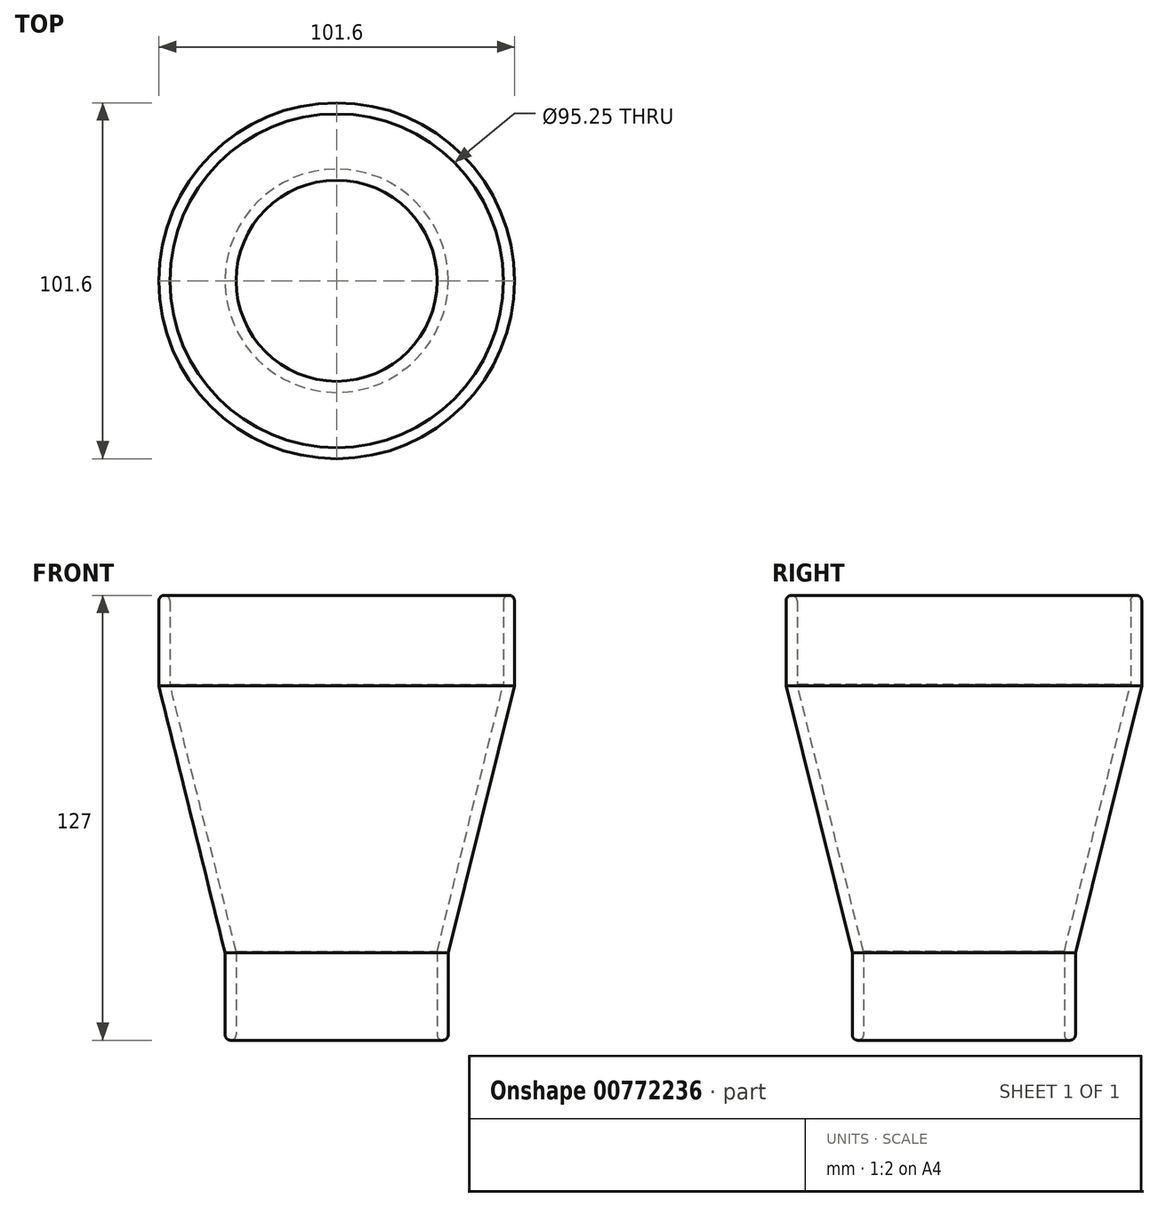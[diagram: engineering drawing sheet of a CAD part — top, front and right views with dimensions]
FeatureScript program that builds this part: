
annotation { "Feature Type Name" : "Feature", "Feature Type Description" : "" }
export const myFeature = defineFeature(function(context is Context, id is Id, definition is map)
    precondition{}
    {
        {
            var Q0;
            Q0=qCreatedBy(makeId("Front.planeOp"),FACE);
            var sketch = newSketch(context, id + "F0", { "sketchPlane" : qUnion([Q0])});
            skLineSegment(sketch, "E0", {"start": v(0, 0) * mm, "end": v(0, 101.6) * mm});
            skLineSegment(sketch, "E1", {"start": v(0, 0) * mm, "end": v(31.88, 0) * mm});
            skLineSegment(sketch, "E2", {"start": v(0, 101.6) * mm, "end": v(47.63, 101.6) * mm});
            skLineSegment(sketch, "E3", {"start": v(28.7, 0) * mm, "end": v(28.7, 25.4) * mm});
            skLineSegment(sketch, "E4", {"start": v(28.7, 25.4) * mm, "end": v(47.63, 101.6) * mm});
            skLineSegment(sketch, "E5", {"start": v(47.63, 101.6) * mm, "end": v(47.63, 127) * mm});
            skLineSegment(sketch, "E6", {"start": v(50.8, 127) * mm, "end": v(0, 127) * mm});
            skLineSegment(sketch, "E7", {"start": v(0, 127) * mm, "end": v(0, 101.6) * mm});
            skLineSegment(sketch, "E8.0", {"start": v(50.8, 101.21) * mm, "end": v(50.8, 127) * mm});
            skLineSegment(sketch, "E8.1", {"start": v(31.88, 25.01) * mm, "end": v(50.8, 101.21) * mm});
            skLineSegment(sketch, "E8.2", {"start": v(31.88, 0) * mm, "end": v(31.88, 25.01) * mm});
            skSolve(sketch);
        }
        {
            var Q0;
            {var subQ1=sQuery(id+"F0.wireOp",EDGE,"E3");Q0=makeQuery(id+"F0.imprint","IMPRINT",FACE,{"disambiguationData":[TD([[makeQuery(id+"F0.imprint","IMPRINT",EDGE,{"derivedFrom":subQ1}),-1.0]])]});}
            var Q1;
            Q1=sQuery(id+"F0.wireOp",EDGE,"E0");
            revolve(context, id + "F1", {"surfaceOperationType" : NewSurfaceOperationType.NEW, "entities" : qUnion([Q0]), "axis" : qUnion([Q1]), "revolveType" : RevolveType.FULL});
        }
        {
            var Q0;
            Q0=qCreatedBy(makeId("Right.planeOp"),FACE);
            var sketch = newSketch(context, id + "F2", { "sketchPlane" : qUnion([Q0])});
            skLineSegment(sketch, "E9", {"start": v(9.53, 0) * mm, "end": v(9.53, 10.03) * mm});
            skLineSegment(sketch, "E10", {"start": v(6.35, 13.2) * mm, "end": v(-2.78, 13.2) * mm});
            skLineSegment(sketch, "E11", {"start": v(-2.78, 5.27) * mm, "end": v(0, 5.27) * mm});
            skLineSegment(sketch, "E12", {"start": v(0, 5.27) * mm, "end": v(0, 0) * mm});
            skArc(sketch, "E13", {"start": v(-3.63, 12.7) * mm, "mid": v(-9.52, 9.18) * mm, "end": v(-3.53, 5.83) * mm});
            skLineSegment(sketch, "E14", {"start": v(-3.53, 5.83) * mm, "end": v(-2.78, 5.27) * mm});
            skLineSegment(sketch, "E15", {"start": v(-3.63, 12.7) * mm, "end": v(-2.78, 13.2) * mm});
            skPoint(sketch, "E16.orphan", {"position": v(-5.56, 5.27) * mm});
            skPoint(sketch, "E17.visualSharp", {"position": v(9.53, 13.2) * mm});
            skArc(sketch, "E17.filletArc", {"start": v(9.53, 10.03) * mm, "mid": v(8.6, 12.28) * mm, "end": v(6.35, 13.2) * mm});
            skLineSegment(sketch, "E18", {"start": v(0, 0) * mm, "end": v(9.53, 0) * mm});
            skSolve(sketch);
        }
        {
            var Q0;
            Q0=qSketchRegion(id+"F2",true);
            extrude(context, id + "F3", {"entities" : qUnion([Q0]), "operationType" : NewBodyOperationType.REMOVE, "oppositeDirection" : true, "depth" : 25.4 * mm, "offsetDistance" : 25.4 * mm});
        }
        {
            var Q0;
            Q0=qCreatedBy(makeId("Right.planeOp"),FACE);
            var sketch = newSketch(context, id + "F4", { "sketchPlane" : qUnion([Q0])});
            skLineSegment(sketch, "E19", {"start": v(-9.52, -0.13) * mm, "end": v(-9.52, 9.9) * mm});
            skLineSegment(sketch, "E20.MirrorCS", {"start": v(3.53, 5.7) * mm, "end": v(2.78, 5.14) * mm});
            skLineSegment(sketch, "E21.MirrorCS", {"start": v(3.63, 12.58) * mm, "end": v(2.78, 13.08) * mm});
            skLineSegment(sketch, "E22.MirrorCS", {"start": v(2.78, 5.14) * mm, "end": v(0, 5.14) * mm});
            skArc(sketch, "E23.MirrorCS", {"start": v(-9.52, 9.9) * mm, "mid": v(-8.6, 12.15) * mm, "end": v(-6.35, 13.08) * mm});
            skLineSegment(sketch, "E24.MirrorCS", {"start": v(-6.35, 13.08) * mm, "end": v(2.78, 13.08) * mm});
            skLineSegment(sketch, "E25.MirrorCS", {"start": v(0, 5.14) * mm, "end": v(0, -0.13) * mm});
            skArc(sketch, "E26.MirrorCS", {"start": v(3.63, 12.58) * mm, "mid": v(9.53, 9.05) * mm, "end": v(3.53, 5.7) * mm});
            skLineSegment(sketch, "E27.MirrorCS", {"start": v(0, -0.13) * mm, "end": v(-9.52, -0.13) * mm});
            skPoint(sketch, "E28.MirrorP", {"position": v(5.56, 5.14) * mm});
            skSolve(sketch);
        }
        {
            var Q0;
            Q0=qSketchRegion(id+"F4",true);
            extrude(context, id + "F5", {"entities" : qUnion([Q0]), "operationType" : NewBodyOperationType.REMOVE, "depth" : 25.4 * mm, "offsetDistance" : 25.4 * mm});
        }
        {
            var Q0;
            {var subQ0=sQuery(id+"F0.wireOp",EDGE,"E1");var subQ1=sQuery(id+"F0.wireOp",EDGE,"E8.2");Q0=makeQuery(id+"F5.boolean.opBoolean","SPLIT",EDGE,{"disambiguationData":[TD([makeQuery(id+"F3.boolean.opBoolean","COPY",FACE,{"derivedFrom":makeQuery(id+"F3.opExtrude","SWEPT_FACE",FACE,{"disambiguationData":[OSD([sQuery(id+"F2.wireOp",EDGE,"E12")])]})})])],"derivedFrom":makeQuery(id+"F1.opRevolve","SWEPT_EDGE",EDGE,{"disambiguationData":[OSD([subQ0,subQ1])]})});}
            var Q1;
            {var subQ0=sQuery(id+"F0.wireOp",EDGE,"E1");var subQ1=sQuery(id+"F0.wireOp",EDGE,"E8.2");Q1=makeQuery(id+"F5.boolean.opBoolean","SPLIT",EDGE,{"disambiguationData":[TD([makeQuery(id+"F3.boolean.opBoolean","COPY",FACE,{"derivedFrom":makeQuery(id+"F3.opExtrude","SWEPT_FACE",FACE,{"disambiguationData":[OSD([sQuery(id+"F2.wireOp",EDGE,"E9")])]})})])],"derivedFrom":makeQuery(id+"F1.opRevolve","SWEPT_EDGE",EDGE,{"disambiguationData":[OSD([subQ0,subQ1])]})});}
            var Q2;
            Q2=makeQuery(id+"F1.opRevolve","SWEPT_EDGE",EDGE,{"disambiguationData":[OSD([sQuery(id+"F0.wireOp",EDGE,"E6"),sQuery(id+"F0.wireOp",EDGE,"E8.0")])]});
            var Q3;
            {var subQ0=sQuery(id+"F0.wireOp",EDGE,"E1");var subQ1=sQuery(id+"F0.wireOp",EDGE,"E3");Q3=makeQuery(id+"F5.boolean.opBoolean","SPLIT",EDGE,{"disambiguationData":[TD([makeQuery(id+"F3.boolean.opBoolean","COPY",FACE,{"derivedFrom":makeQuery(id+"F3.opExtrude","SWEPT_FACE",FACE,{"disambiguationData":[OSD([sQuery(id+"F2.wireOp",EDGE,"E12")])]})})])],"derivedFrom":makeQuery(id+"F1.opRevolve","SWEPT_EDGE",EDGE,{"disambiguationData":[OSD([subQ0,subQ1])]})});}
            var Q4;
            Q4=makeQuery(id+"F1.opRevolve","SWEPT_EDGE",EDGE,{"disambiguationData":[OSD([sQuery(id+"F0.wireOp",EDGE,"E5"),sQuery(id+"F0.wireOp",EDGE,"E6")])]});
            fillet(context, id + "F6", {"entities" : qUnion([Q0, Q1, Q2, Q3, Q4]), "radius" : 1.59 * mm, "tangentPropagation" : true, "allowEdgeOverflow" : false});
        }
    });
